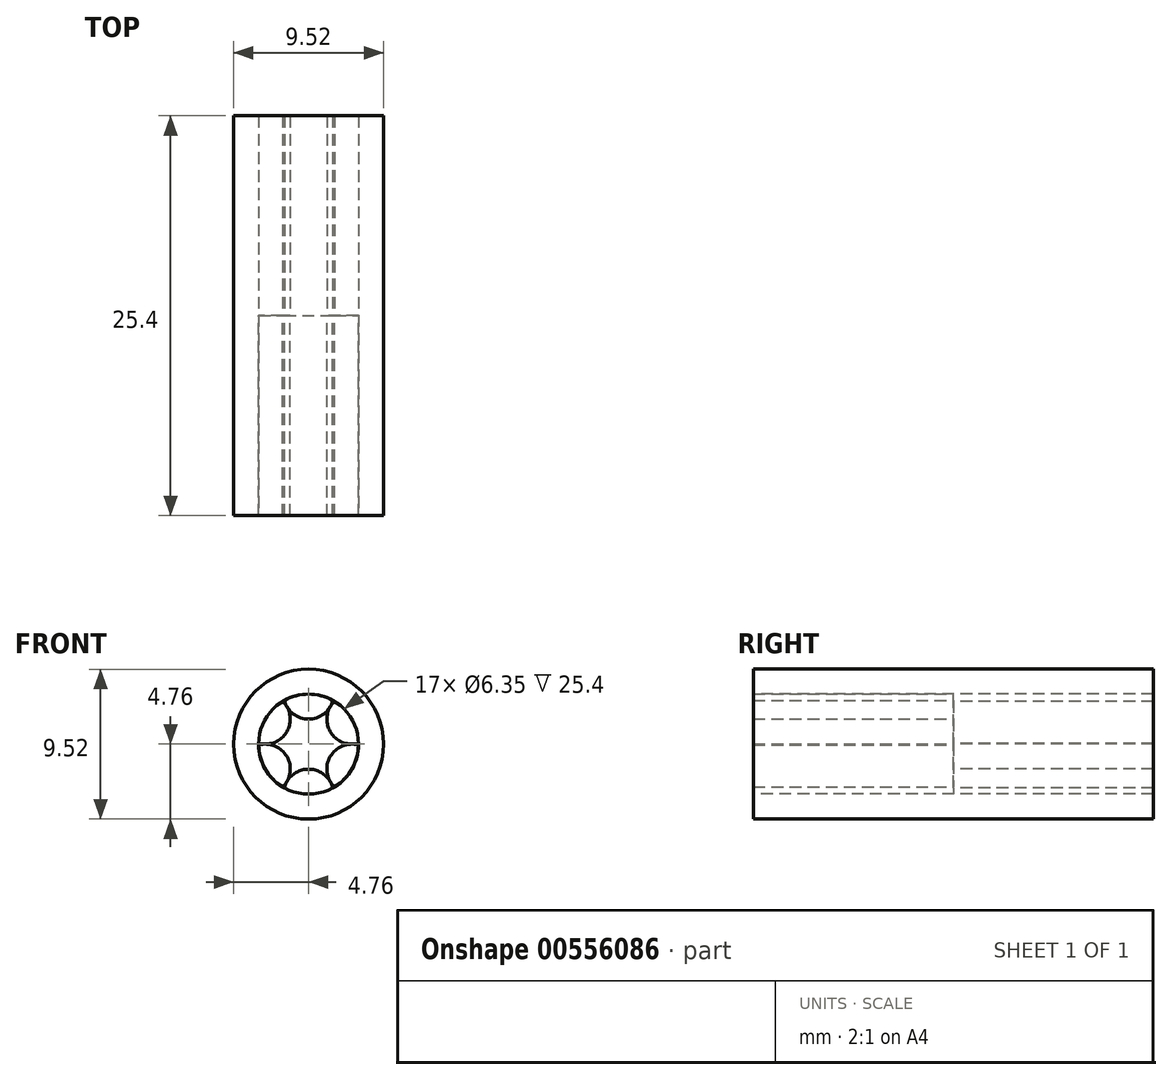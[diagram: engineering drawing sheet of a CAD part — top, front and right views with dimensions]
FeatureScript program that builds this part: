
annotation { "Feature Type Name" : "Feature", "Feature Type Description" : "" }
export const myFeature = defineFeature(function(context is Context, id is Id, definition is map)
    precondition{}
    {
        {
            var Q0;
            Q0=qCreatedBy(makeId("Front.planeOp"),FACE);
            var sketch = newSketch(context, id + "F0", { "sketchPlane" : qUnion([Q0])});
            skCircle(sketch, "E0", {"center": v(0, 0) * mm, "radius": 4.76 * mm});
            skCircle(sketch, "E1", {"center": v(0, 0) * mm, "radius": 3.18 * mm});
            skLineSegment(sketch, "E2", {"start": v(0, 0) * mm, "end": v(0, 3.18) * mm});
            skCircle(sketch, "E3", {"center": v(0, 3.18) * mm, "radius": 1.59 * mm});
            skSolve(sketch);
        }
        {
            var Q0;
            {var subQ0=sQuery(id+"F0.wireOp",EDGE,"E2");var subQ1=sQuery(id+"F0.wireOp",EDGE,"E1");var subQ2=makeQuery(id+"F0.imprint","INTERSECT",VERTEX,{"derivedFrom":[subQ1,subQ0]});Q0=makeQuery(id+"F0.imprint","IMPRINT",FACE,{"disambiguationData":[TD([[makeQuery(id+"F0.imprint","IMPRINT",EDGE,{"disambiguationData":[TD([[subQ2,-1.0]])],"derivedFrom":subQ1}),1.0]])]});}
            var Q1;
            {var subQ0=sQuery(id+"F0.wireOp",EDGE,"E2");var subQ1=sQuery(id+"F0.wireOp",EDGE,"E1");var subQ2=makeQuery(id+"F0.imprint","INTERSECT",VERTEX,{"derivedFrom":[subQ1,subQ0]});Q1=makeQuery(id+"F0.imprint","IMPRINT",FACE,{"disambiguationData":[TD([[makeQuery(id+"F0.imprint","IMPRINT",EDGE,{"disambiguationData":[TD([[subQ2,1.0]])],"derivedFrom":subQ1}),1.0]])]});}
            extrude(context, id + "F1", {"entities" : qUnion([Q0, Q1]), "depth" : 12.7 * mm, "offsetDistance" : 25.4 * mm});
        }
        {
            var Q0;
            Q0=qCreatedBy(makeId("Right.planeOp"),FACE);
            var sketch = newSketch(context, id + "F2", { "sketchPlane" : qUnion([Q0])});
            skLineSegment(sketch, "E4", {"start": v(0, 0) * mm, "end": v(-3, 0) * mm});
            skSolve(sketch);
        }
        {
            var Q0;
            Q0=makeQuery(id+"F1.opExtrude","SWEPT_BODY",BODY,{"disambiguationData":[OSD([sQuery(id+"F0.wireOp",EDGE,"E1"),sQuery(id+"F0.wireOp",EDGE,"E3")])]});
            var Q1;
            Q1=sQuery(id+"F2.wireOp",EDGE,"E4");
            circularPattern(context, id + "F3", {"entities" : qUnion([Q0]), "axis" : qUnion([Q1]), "angle" : 360 * degree, "instanceCount" : 3, "equalSpace" : true});
        }
        {
            var Q0;
            Q0=qCreatedBy(makeId("Front.planeOp"),FACE);
            var sketch = newSketch(context, id + "F4", { "sketchPlane" : qUnion([Q0])});
            skCircle(sketch, "E5", {"center": v(0, 0) * mm, "radius": 3.18 * mm});
            skCircle(sketch, "E6", {"center": v(0, 0) * mm, "radius": 4.76 * mm});
            skLineSegment(sketch, "E7", {"start": v(0, 0) * mm, "end": v(-3.18, 0) * mm});
            skLineSegment(sketch, "E8", {"start": v(0, 0) * mm, "end": v(0, 3.18) * mm});
            skLineSegment(sketch, "E9", {"start": v(0, 0) * mm, "end": v(-2.75, 1.59) * mm});
            skCircle(sketch, "E10", {"center": v(-2.75, 1.59) * mm, "radius": 1.59 * mm});
            skSolve(sketch);
        }
        {
            var Q0;
            {var subQ0=sQuery(id+"F0.wireOp",EDGE,"E0");Q0=makeQuery(id+"F0.imprint","IMPRINT",FACE,{"disambiguationData":[TD([[makeQuery(id+"F0.imprint","IMPRINT",EDGE,{"derivedFrom":subQ0}),1.0]])]});}
            var Q1;
            {var subQ0=sQuery(id+"F0.wireOp",EDGE,"E1");var subQ1=makeQuery(id+"F0.imprint","INTERSECT",VERTEX,{"derivedFrom":[subQ0,sQuery(id+"F0.wireOp",EDGE,"E2")]});Q1=makeQuery(id+"F0.imprint","IMPRINT",FACE,{"disambiguationData":[TD([[makeQuery(id+"F0.imprint","IMPRINT",EDGE,{"disambiguationData":[TD([[subQ1,1.0]])],"derivedFrom":subQ0}),-1.0]])]});}
            extrude(context, id + "F5", {"entities" : qUnion([Q0, Q1]), "endBound" : BoundingType.SYMMETRIC, "oppositeDirection" : true, "depth" : 25.4 * mm, "offsetDistance" : 25.4 * mm});
        }
        {
            var Q0;
            {var subQ0=sQuery(id+"F4.wireOp",EDGE,"E9");var subQ1=sQuery(id+"F4.wireOp",EDGE,"E5");var subQ2=makeQuery(id+"F4.imprint","INTERSECT",VERTEX,{"derivedFrom":[subQ1,subQ0]});Q0=makeQuery(id+"F4.imprint","IMPRINT",FACE,{"disambiguationData":[TD([[makeQuery(id+"F4.imprint","IMPRINT",EDGE,{"disambiguationData":[TD([[subQ2,1.0]])],"derivedFrom":subQ1}),1.0]])]});}
            var Q1;
            {var subQ0=sQuery(id+"F4.wireOp",EDGE,"E9");var subQ1=sQuery(id+"F4.wireOp",EDGE,"E5");var subQ2=makeQuery(id+"F4.imprint","INTERSECT",VERTEX,{"derivedFrom":[subQ1,subQ0]});Q1=makeQuery(id+"F4.imprint","IMPRINT",FACE,{"disambiguationData":[TD([[makeQuery(id+"F4.imprint","IMPRINT",EDGE,{"disambiguationData":[TD([[subQ2,-1.0]])],"derivedFrom":subQ1}),1.0]])]});}
            extrude(context, id + "F6", {"entities" : qUnion([Q0, Q1]), "oppositeDirection" : true, "depth" : 12.7 * mm, "offsetDistance" : 25.4 * mm});
        }
        {
            var Q0;
            Q0=makeQuery(id+"F6.opExtrude","SWEPT_BODY",BODY,{"disambiguationData":[OSD([sQuery(id+"F4.wireOp",EDGE,"E5"),sQuery(id+"F4.wireOp",EDGE,"E10")])]});
            var Q1;
            Q1=sQuery(id+"F2.wireOp",EDGE,"E4");
            circularPattern(context, id + "F7", {"entities" : qUnion([Q0]), "axis" : qUnion([Q1]), "angle" : 360 * degree, "instanceCount" : 3, "equalSpace" : true});
        }
    });
